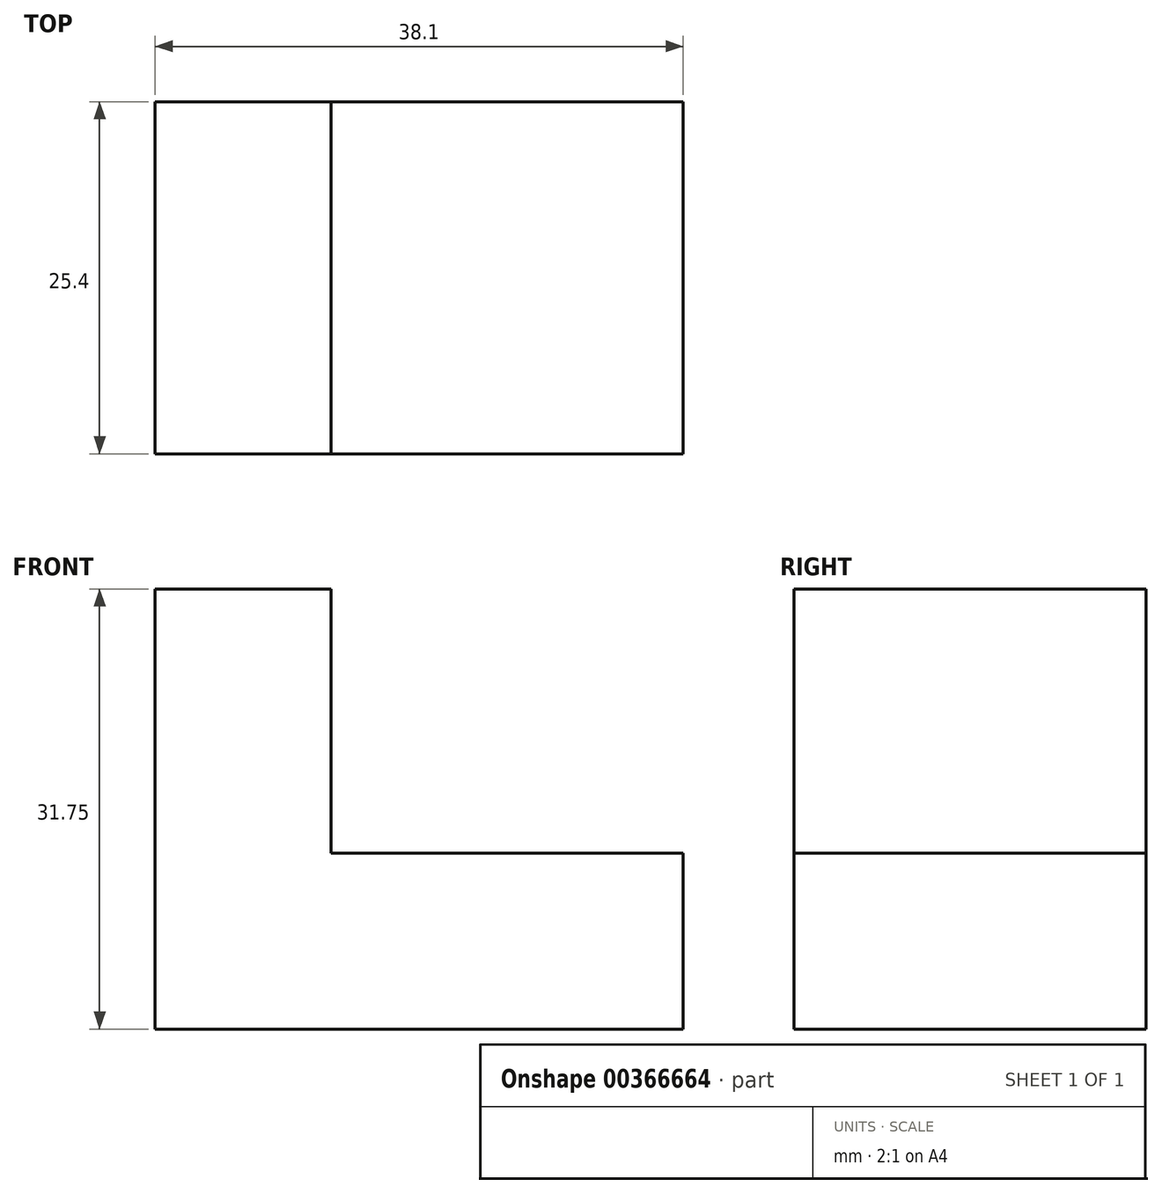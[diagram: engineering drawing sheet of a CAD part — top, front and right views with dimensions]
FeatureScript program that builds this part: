
annotation { "Feature Type Name" : "Feature", "Feature Type Description" : "" }
export const myFeature = defineFeature(function(context is Context, id is Id, definition is map)
    precondition{}
    {
        {
            var Q0;
            Q0=qCreatedBy(makeId("Front.planeOp"),FACE);
            var sketch = newSketch(context, id + "F0", { "sketchPlane" : qUnion([Q0])});
            skLineSegment(sketch, "E0", {"start": v(-45.81, 31.75) * mm, "end": v(-45.81, 0) * mm});
            skLineSegment(sketch, "E1", {"start": v(-45.81, 0) * mm, "end": v(-7.71, 0) * mm});
            skLineSegment(sketch, "E2", {"start": v(-45.81, 31.75) * mm, "end": v(-33.11, 31.75) * mm});
            skLineSegment(sketch, "E3", {"start": v(-33.11, 31.75) * mm, "end": v(-33.11, 12.7) * mm});
            skLineSegment(sketch, "E4", {"start": v(-33.11, 12.7) * mm, "end": v(-7.71, 12.7) * mm});
            skLineSegment(sketch, "E5", {"start": v(-7.71, 12.7) * mm, "end": v(-7.71, 0) * mm});
            skSolve(sketch);
        }
        {
            var Q0;
            Q0=makeQuery(id+"F0.imprint","IMPRINT",FACE,{"disambiguationData":[TD([[makeQuery(id+"F0.imprint","IMPRINT",EDGE,{"derivedFrom":sQuery(id+"F0.wireOp",EDGE,"E0")}),1.0]])]});
            extrude(context, id + "F1", {"entities" : qUnion([Q0]), "depth" : 25.4 * mm});
        }
    });
